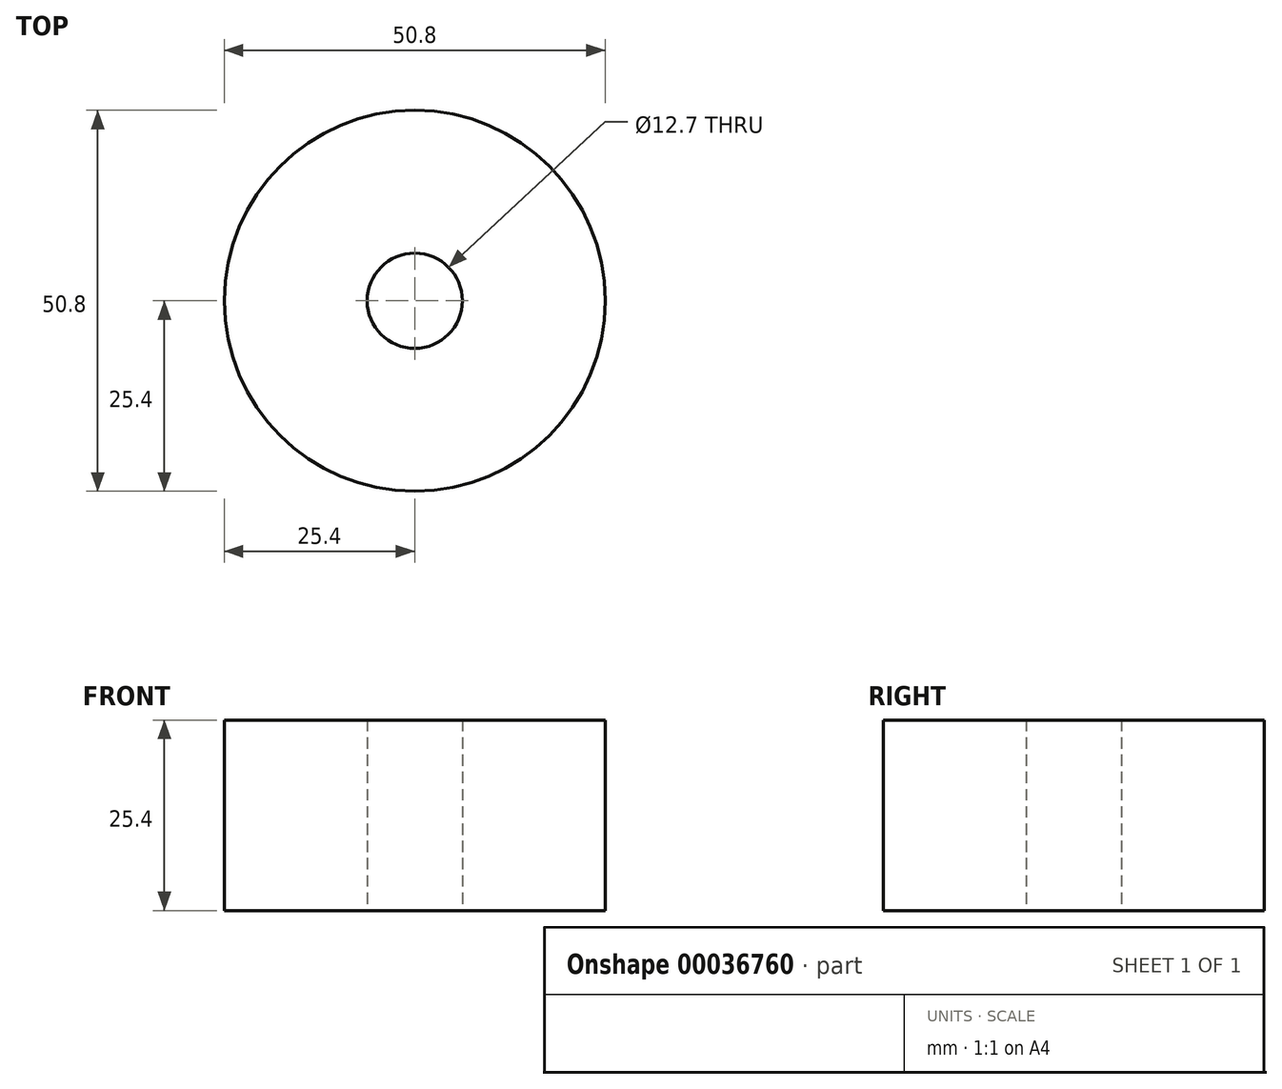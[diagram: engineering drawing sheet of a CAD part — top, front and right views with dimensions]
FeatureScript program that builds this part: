
annotation { "Feature Type Name" : "Feature", "Feature Type Description" : "" }
export const myFeature = defineFeature(function(context is Context, id is Id, definition is map)
    precondition{}
    {
        {
            var Q0;
            Q0=qCreatedBy(makeId("Top.planeOp"),FACE);
            var sketch = newSketch(context, id + "F0", { "sketchPlane" : qUnion([Q0])});
            skCircle(sketch, "E0", {"center": v(0, 0) * mm, "radius": 25.4 * mm});
            skCircle(sketch, "E1", {"center": v(0, 0) * mm, "radius": 6.35 * mm});
            skSolve(sketch);
        }
        {
            var Q0;
            Q0=makeQuery(id+"F0.imprint","IMPRINT",FACE,{"disambiguationData":[TD([[makeQuery(id+"F0.imprint","IMPRINT",EDGE,{"derivedFrom":sQuery(id+"F0.wireOp",EDGE,"E0")}),1.0]])]});
            extrude(context, id + "F1", {"entities" : qUnion([Q0]), "depth" : 25.4 * mm});
        }
    });
